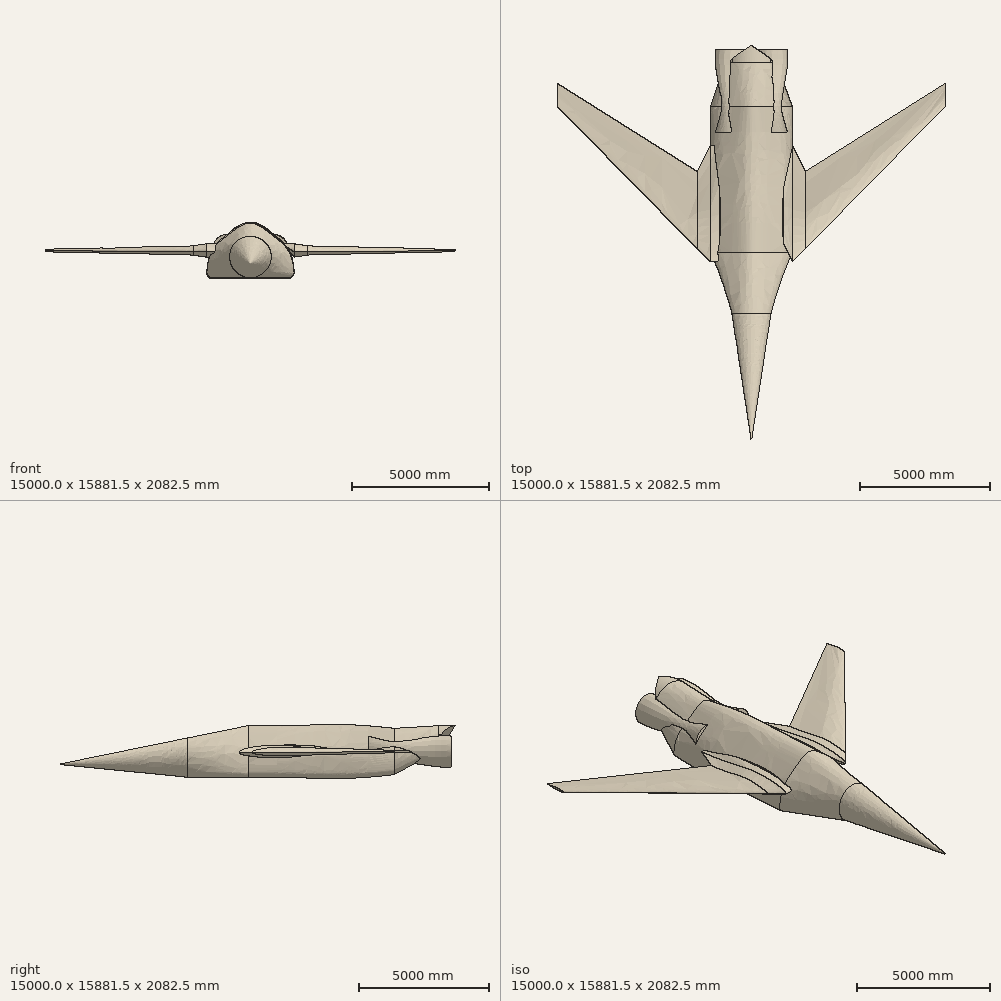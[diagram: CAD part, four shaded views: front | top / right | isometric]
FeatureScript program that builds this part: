
annotation { "Feature Type Name" : "Feature", "Feature Type Description" : "" }
export const myFeature = defineFeature(function(context is Context, id is Id, definition is map)
    precondition{}
    {
        {
            var Q0;
            Q0=qCreatedBy(makeId("Right.planeOp"),FACE);
            var sketch = newSketch(context, id + "F0", { "sketchPlane" : qUnion([Q0])});
            skLineSegment(sketch, "E0", {"start": v(0, 0) * mm, "end": v(-1750, 0) * mm});
            skLineSegment(sketch, "E1", {"start": v(-1750, 0) * mm, "end": v(-3500, 0) * mm});
            skLineSegment(sketch, "E2", {"start": v(-3500, 0) * mm, "end": v(-3500, -1000) * mm});
            skLineSegment(sketch, "E3", {"start": v(-3500, -1000) * mm, "end": v(-8500, -1000) * mm});
            skLineSegment(sketch, "E4", {"start": v(-8500, -1000) * mm, "end": v(-8500, -499.31) * mm});
            skLineSegment(sketch, "E5", {"start": v(-1151.4, 0) * mm, "end": v(-1151.4, 1000) * mm});
            skLineSegment(sketch, "E6", {"start": v(-1151.4, 1000) * mm, "end": v(-8500, -499.31) * mm});
            skLineSegment(sketch, "E7", {"start": v(-8500, -499.31) * mm, "end": v(-3500, -1000) * mm});
            skLineSegment(sketch, "E8", {"start": v(-3500, 0) * mm, "end": v(-3500, 520.82) * mm});
            skLineSegment(sketch, "E9", {"start": v(-8500, -499.31) * mm, "end": v(-8450, -499.31) * mm});
            skLineSegment(sketch, "E10", {"start": v(-8450, -499.31) * mm, "end": v(-8450, -489.1) * mm});
            skLineSegment(sketch, "E11", {"start": v(-8450, -499.31) * mm, "end": v(-8450, -504.32) * mm});
            skSolve(sketch);
        }
        {
            var Q0;
            Q0=sQuery(id+"F0.wireOp",EDGE,"E5");
            cPlane(context, id + "F1", {"entities" : qUnion([Q0]), "cplaneType" : CPlaneType.LINE_ANGLE, "offset" : 25 * mm, "angle" : 90 * degree, "oppositeDirection" : true, "width" : 150 * mm, "height" : 150 * mm});
        }
        {
            var Q0;
            Q0=qCreatedBy(id+"F1.planeOp",FACE);
            var sketch = newSketch(context, id + "F2", { "sketchPlane" : qUnion([Q0])});
            skLineSegment(sketch, "E12.top", {"start": v(-1394.2, -1000) * mm, "end": v(1394.2, -1000) * mm});
            skPoint(sketch, "E12.middle", {"position": v(0, 0) * mm});
            skFitSpline(sketch, "E13", {"points": [v(-1600, -1000) * mm, v(-848, 530) * mm, v(0, 1000) * mm, v(848, 530) * mm, v(1600, -1000) * mm], "startDerivative": vector(0, 10524.75) * mm, "endDerivative": vector(0, -10524.75) * mm});
            skArc(sketch, "E14", {"start": v(-735.27, 618.52) * mm, "mid": v(-1273.27, 435.52) * mm, "end": v(-1440.68, -107.53) * mm});
            skArc(sketch, "E15", {"start": v(1440.68, -107.53) * mm, "mid": v(1273.27, 435.52) * mm, "end": v(735.27, 618.52) * mm});
            skFitSpline(sketch, "E16.trimOffspring", {"points": [v(-1600, -1000) * mm, v(-848, 530) * mm, v(0, 1000) * mm, v(848, 530) * mm, v(1600, -1000) * mm], "startDerivative": vector(0, 10524.75) * mm, "endDerivative": vector(0, -10524.75) * mm});
            skFitSpline(sketch, "E17.trimOffspring", {"points": [v(-1600, -1000) * mm, v(-848, 530) * mm, v(0, 1000) * mm, v(848, 530) * mm, v(1600, -1000) * mm], "startDerivative": vector(0, 10524.75) * mm, "endDerivative": vector(0, -10524.75) * mm});
            skArc(sketch, "E18.filletArc", {"start": v(-1593.82, -787.83) * mm, "mid": v(-1539.85, -937.05) * mm, "end": v(-1394.2, -1000) * mm});
            skArc(sketch, "E19.filletArc", {"start": v(1394.2, -1000) * mm, "mid": v(1539.85, -937.05) * mm, "end": v(1593.82, -787.83) * mm});
            skSolve(sketch);
        }
        {
            var Q0;
            Q0=qCreatedBy(makeId("Front.planeOp"),FACE);
            var sketch = newSketch(context, id + "F3", { "sketchPlane" : qUnion([Q0])});
            skLineSegment(sketch, "E20.top", {"start": v(-1394.2, -1000) * mm, "end": v(1394.2, -1000) * mm});
            skPoint(sketch, "E20.middle", {"position": v(0, 0) * mm});
            skFitSpline(sketch, "E21", {"points": [v(-1600, -1000) * mm, v(-848, 530) * mm, v(0, 1000) * mm, v(848, 530) * mm, v(1600, -1000) * mm], "startDerivative": vector(0, 10524.75) * mm, "endDerivative": vector(0, -10524.75) * mm});
            skArc(sketch, "E22", {"start": v(-735.27, 618.52) * mm, "mid": v(-1273.27, 435.52) * mm, "end": v(-1440.68, -107.53) * mm});
            skArc(sketch, "E23", {"start": v(1440.68, -107.53) * mm, "mid": v(1273.27, 435.52) * mm, "end": v(735.27, 618.52) * mm});
            skFitSpline(sketch, "E24.trimOffspring", {"points": [v(-1600, -1000) * mm, v(-848, 530) * mm, v(0, 1000) * mm, v(848, 530) * mm, v(1600, -1000) * mm], "startDerivative": vector(0, 10524.75) * mm, "endDerivative": vector(0, -10524.75) * mm});
            skFitSpline(sketch, "E25.trimOffspring", {"points": [v(-1600, -1000) * mm, v(-848, 530) * mm, v(0, 1000) * mm, v(848, 530) * mm, v(1600, -1000) * mm], "startDerivative": vector(0, 10524.75) * mm, "endDerivative": vector(0, -10524.75) * mm});
            skArc(sketch, "E26.filletArc", {"start": v(-1593.82, -787.83) * mm, "mid": v(-1539.85, -937.05) * mm, "end": v(-1394.2, -1000) * mm});
            skArc(sketch, "E27.filletArc", {"start": v(1394.2, -1000) * mm, "mid": v(1539.85, -937.05) * mm, "end": v(1593.82, -787.83) * mm});
            skSolve(sketch);
        }
        {
            var Q0;
            Q0=qCreatedBy(makeId("Front.planeOp"),FACE);
            cPlane(context, id + "F4", {"entities" : qUnion([Q0]), "cplaneType" : CPlaneType.OFFSET, "offset" : 3500 * mm, "oppositeDirection" : true, "width" : 150 * mm, "height" : 150 * mm});
        }
        {
            var Q0;
            Q0=qCreatedBy(id+"F4.planeOp",FACE);
            var sketch = newSketch(context, id + "F5", { "sketchPlane" : qUnion([Q0])});
            skLineSegment(sketch, "E28.top", {"start": v(-1394.2, -1000) * mm, "end": v(1394.2, -1000) * mm});
            skPoint(sketch, "E28.middle", {"position": v(0, 0) * mm});
            skFitSpline(sketch, "E29", {"points": [v(-1600, -1000) * mm, v(-848, 530) * mm, v(0, 1000) * mm, v(848, 530) * mm, v(1600, -1000) * mm], "startDerivative": vector(0, 10524.75) * mm, "endDerivative": vector(0, -10524.75) * mm});
            skArc(sketch, "E30", {"start": v(-735.27, 618.52) * mm, "mid": v(-1273.27, 435.52) * mm, "end": v(-1440.68, -107.53) * mm});
            skArc(sketch, "E31", {"start": v(1440.68, -107.53) * mm, "mid": v(1273.27, 435.52) * mm, "end": v(735.27, 618.52) * mm});
            skFitSpline(sketch, "E32.trimOffspring", {"points": [v(-1600, -1000) * mm, v(-848, 530) * mm, v(0, 1000) * mm, v(848, 530) * mm, v(1600, -1000) * mm], "startDerivative": vector(0, 10524.75) * mm, "endDerivative": vector(0, -10524.75) * mm});
            skFitSpline(sketch, "E33.trimOffspring", {"points": [v(-1600, -1000) * mm, v(-848, 530) * mm, v(0, 1000) * mm, v(848, 530) * mm, v(1600, -1000) * mm], "startDerivative": vector(0, 10524.75) * mm, "endDerivative": vector(0, -10524.75) * mm});
            skArc(sketch, "E34.filletArc", {"start": v(-1593.82, -787.83) * mm, "mid": v(-1539.85, -937.05) * mm, "end": v(-1394.2, -1000) * mm});
            skArc(sketch, "E35.filletArc", {"start": v(1394.2, -1000) * mm, "mid": v(1539.85, -937.05) * mm, "end": v(1593.82, -787.83) * mm});
            skSolve(sketch);
        }
        {
            var Q0;
            Q0=qCreatedBy(makeId("Front.planeOp"),FACE);
            cPlane(context, id + "F6", {"entities" : qUnion([Q0]), "cplaneType" : CPlaneType.OFFSET, "offset" : 4500 * mm, "oppositeDirection" : true, "width" : 150 * mm, "height" : 150 * mm});
        }
        {
            var Q0;
            Q0=qCreatedBy(id+"F6.planeOp",FACE);
            var sketch = newSketch(context, id + "F7", { "sketchPlane" : qUnion([Q0])});
            skLineSegment(sketch, "E36.top", {"start": v(-1413.07, -900) * mm, "end": v(1413.07, -900) * mm});
            skPoint(sketch, "E36.middle", {"position": v(0, 0) * mm});
            skFitSpline(sketch, "E37", {"points": [v(-1600, -900) * mm, v(-784.42, 441.24) * mm, v(0, 900) * mm, v(784.42, 441.24) * mm, v(1600, -900) * mm], "startDerivative": vector(0, 9508.62) * mm, "endDerivative": vector(0, -9508.62) * mm});
            skArc(sketch, "E38", {"start": v(-719.25, 488.69) * mm, "mid": v(-1131.76, 394.84) * mm, "end": v(-1324.66, 18.33) * mm});
            skArc(sketch, "E39", {"start": v(1324.66, 18.33) * mm, "mid": v(1131.76, 394.84) * mm, "end": v(719.25, 488.69) * mm});
            skFitSpline(sketch, "E40.trimOffspring", {"points": [v(-1600, -900) * mm, v(-784.42, 441.24) * mm, v(0, 900) * mm, v(784.42, 441.24) * mm, v(1600, -900) * mm], "startDerivative": vector(0, 9508.62) * mm, "endDerivative": vector(0, -9508.62) * mm});
            skFitSpline(sketch, "E41.trimOffspring", {"points": [v(-1600, -900) * mm, v(-784.42, 441.24) * mm, v(0, 900) * mm, v(784.42, 441.24) * mm, v(1600, -900) * mm], "startDerivative": vector(0, 9508.62) * mm, "endDerivative": vector(0, -9508.62) * mm});
            skArc(sketch, "E42.filletArc", {"start": v(-1592.48, -705.43) * mm, "mid": v(-1545.4, -842.02) * mm, "end": v(-1413.07, -900) * mm});
            skArc(sketch, "E43.filletArc", {"start": v(1413.07, -900) * mm, "mid": v(1545.4, -842.02) * mm, "end": v(1592.48, -705.43) * mm});
            skLineSegment(sketch, "E44", {"start": v(-719.25, 488.69) * mm, "end": v(-1324.66, 18.33) * mm, "construction": true});
            skLineSegment(sketch, "E45", {"start": v(719.25, 488.69) * mm, "end": v(1324.66, 18.33) * mm, "construction": true});
            skSolve(sketch);
        }
        {
            var Q0;
            Q0=qCreatedBy(makeId("Front.planeOp"),FACE);
            cPlane(context, id + "F8", {"entities" : qUnion([Q0]), "cplaneType" : CPlaneType.OFFSET, "offset" : 6232.05 * mm, "oppositeDirection" : true, "width" : 150 * mm, "height" : 150 * mm});
        }
        {
            var Q0;
            Q0=qCreatedBy(id+"F8.planeOp",FACE);
            var sketch = newSketch(context, id + "F9", { "sketchPlane" : qUnion([Q0])});
            skArc(sketch, "E46", {"start": v(998.61, 52.63) * mm, "mid": v(0, 1000) * mm, "end": v(-998.61, 52.63) * mm});
            skLineSegment(sketch, "E47", {"start": v(0, 0) * mm, "end": v(-948.68, 0) * mm});
            skLineSegment(sketch, "E48", {"start": v(0, 0) * mm, "end": v(948.68, 0) * mm});
            skLineSegment(sketch, "E49", {"start": v(0, 1000) * mm, "end": v(0, 675) * mm, "construction": true});
            skLineSegment(sketch, "E50", {"start": v(0, 675) * mm, "end": v(-737.82, 675) * mm, "construction": true});
            skLineSegment(sketch, "E51", {"start": v(0, 675) * mm, "end": v(737.82, 675) * mm, "construction": true});
            skPoint(sketch, "E52.visualSharp", {"position": v(-1000, 0) * mm});
            skArc(sketch, "E52.filletArc", {"start": v(-998.61, 52.63) * mm, "mid": v(-984.96, 15.59) * mm, "end": v(-948.68, 0) * mm});
            skPoint(sketch, "E53.visualSharp", {"position": v(1000, 0) * mm});
            skArc(sketch, "E53.filletArc", {"start": v(948.68, 0) * mm, "mid": v(984.96, 15.59) * mm, "end": v(998.61, 52.63) * mm});
            skSolve(sketch);
        }
        {
            var Q0;
            Q0=makeQuery(id+"F2.imprint","IMPRINT",FACE,{"disambiguationData":[TD([[makeQuery(id+"F2.imprint","IMPRINT",EDGE,{"derivedFrom":sQuery(id+"F2.wireOp",EDGE,"E12.top")}),1.0]])]});
            var Q1;
            Q1=makeQuery(id+"F3.imprint","IMPRINT",FACE,{"disambiguationData":[TD([[makeQuery(id+"F3.imprint","IMPRINT",EDGE,{"derivedFrom":sQuery(id+"F3.wireOp",EDGE,"E20.top")}),1.0]])]});
            var Q2;
            Q2=makeQuery(id+"F5.imprint","IMPRINT",FACE,{"disambiguationData":[TD([[makeQuery(id+"F5.imprint","IMPRINT",EDGE,{"derivedFrom":sQuery(id+"F5.wireOp",EDGE,"E28.top")}),1.0]])]});
            var Q3;
            Q3=makeQuery(id+"F7.imprint","IMPRINT",FACE,{"disambiguationData":[TD([[makeQuery(id+"F7.imprint","IMPRINT",EDGE,{"derivedFrom":sQuery(id+"F7.wireOp",EDGE,"E36.top")}),1.0]])]});
            loft(context, id + "F10", {"sheetProfilesArray" : [{ "sheetProfileEntities" : qUnion([Q0]) }, { "sheetProfileEntities" : qUnion([Q1]) }, { "sheetProfileEntities" : qUnion([Q2]) }, { "sheetProfileEntities" : qUnion([Q3]) }]});
        }
        {
            var Q0;
            Q0=sQuery(id+"F7.wireOp",EDGE,"E44");
            var Q1;
            Q1=sQuery(id+"F9.wireOp",VERTEX,"E50.end");
            cPlane(context, id + "F11", {"entities" : qUnion([Q0, Q1]), "cplaneType" : CPlaneType.LINE_ANGLE, "offset" : 25 * mm, "angle" : 180 * degree, "width" : 150 * mm, "height" : 150 * mm});
        }
        {
            var Q0;
            Q0=qCreatedBy(id+"F11.planeOp",FACE);
            var sketch = newSketch(context, id + "F12", { "sketchPlane" : qUnion([Q0])});
            skLineSegment(sketch, "E54", {"start": v(-589.34, 4526.34) * mm, "end": v(-612.8, 6268.32) * mm});
            skLineSegment(sketch, "E55", {"start": v(-1354.08, 4472.19) * mm, "end": v(-612.8, 6268.32) * mm});
            skSolve(sketch);
        }
        {
            var Q0;
            Q0=sQuery(id+"F7.wireOp",EDGE,"E45");
            var Q1;
            Q1=sQuery(id+"F9.wireOp",VERTEX,"E51.end");
            cPlane(context, id + "F13", {"entities" : qUnion([Q0, Q1]), "cplaneType" : CPlaneType.LINE_ANGLE, "offset" : 25 * mm, "angle" : 0 * degree, "width" : 150 * mm, "height" : 150 * mm});
        }
        {
            var Q0;
            Q0=qCreatedBy(id+"F13.planeOp",FACE);
            var sketch = newSketch(context, id + "F14", { "sketchPlane" : qUnion([Q0])});
            skLineSegment(sketch, "E56", {"start": v(589.34, 4526.34) * mm, "end": v(612.8, 6268.32) * mm});
            skLineSegment(sketch, "E57", {"start": v(1354.08, 4472.19) * mm, "end": v(612.8, 6268.32) * mm});
            skSolve(sketch);
        }
        {
            var Q1;
            Q1=makeQuery(id+"F10.opLoft","CAP_FACE",FACE,{"disambiguationData":[OSD([makeQuery(id+"F7.imprint","IMPRINT",FACE,{"disambiguationData":[TD([[makeQuery(id+"F7.imprint","IMPRINT",EDGE,{"derivedFrom":sQuery(id+"F7.wireOp",EDGE,"E36.top")}),1.0]])]})])],"isStart":true});
            var Q2;
            Q2=makeQuery(id+"F9.imprint","IMPRINT",FACE,{"disambiguationData":[TD([[makeQuery(id+"F9.imprint","IMPRINT",EDGE,{"derivedFrom":sQuery(id+"F9.wireOp",EDGE,"E46")}),1.0]])]});
            var Q3;
            Q3=sQuery(id+"F12.wireOp",EDGE,"E54");
            var Q4;
            Q4=sQuery(id+"F14.wireOp",EDGE,"E56");
            loft(context, id + "F15", {"operationType" : NewBodyOperationType.ADD, "addGuides" : true, "sheetProfilesArray" : [{ "sheetProfileEntities" : qUnion([Q1]) }, { "sheetProfileEntities" : qUnion([Q2]) }], "guidesArray" : [{ "guideEntities" : qUnion([Q3]), "guideDerivativeType" : LoftGuideDerivativeType.DEFAULT, "guideDerivativeMagnitude" : 1 }, { "guideEntities" : qUnion([Q4]), "guideDerivativeType" : LoftGuideDerivativeType.DEFAULT, "guideDerivativeMagnitude" : 1 }]});
        }
        {
            var Q0;
            Q0=makeQuery(id+"F15.opLoft","CAP_FACE",FACE,{"disambiguationData":[OSD([makeQuery(id+"F9.imprint","IMPRINT",FACE,{"disambiguationData":[TD([[makeQuery(id+"F9.imprint","IMPRINT",EDGE,{"derivedFrom":sQuery(id+"F9.wireOp",EDGE,"E46")}),1.0]])]})])],"isStart":true});
            extrude(context, id + "F16", {"entities" : qUnion([Q0]), "operationType" : NewBodyOperationType.ADD, "depth" : 649.4 * mm, "offsetDistance" : 25 * mm});
        }
        {
            var Q0;
            Q0=qCreatedBy(makeId("Right.planeOp"),FACE);
            var sketch = newSketch(context, id + "F17", { "sketchPlane" : qUnion([Q0])});
            skLineSegment(sketch, "E58", {"start": v(0, 0) * mm, "end": v(4500, 0) * mm});
            skLineSegment(sketch, "E59", {"start": v(4500, 0) * mm, "end": v(6232.05, 0) * mm});
            skLineSegment(sketch, "E60", {"start": v(4500, 0) * mm, "end": v(4500, 1000) * mm});
            skLineSegment(sketch, "E61", {"start": v(4500, 1000) * mm, "end": v(6881.46, 1000) * mm});
            skLineSegment(sketch, "E62", {"start": v(6881.46, 1000) * mm, "end": v(6881.46, -1000) * mm});
            skLineSegment(sketch, "E63", {"start": v(6881.46, 1000) * mm, "end": v(6232.05, 0) * mm});
            skLineSegment(sketch, "E64", {"start": v(6232.05, 0) * mm, "end": v(5582.64, -1000) * mm});
            skLineSegment(sketch, "E65", {"start": v(5582.64, -1000) * mm, "end": v(6881.46, -1000) * mm});
            skSolve(sketch);
        }
        {
            var Q0;
            Q0=makeQuery(id+"F17.imprint","IMPRINT",FACE,{"disambiguationData":[TD([[makeQuery(id+"F17.imprint","IMPRINT",EDGE,{"derivedFrom":sQuery(id+"F17.wireOp",EDGE,"E62")}),-1.0]])]});
            var Q1;
            Q1=sQuery(id+"F17.wireOp",EDGE,"E61");
            revolve(context, id + "F18", {"operationType" : NewBodyOperationType.REMOVE, "entities" : qUnion([Q0]), "axis" : qUnion([Q1]), "revolveType" : RevolveType.SYMMETRIC, "oppositeDirection" : true, "angle" : 182 * degree});
        }
        {
            var Q0;
            Q0=qCreatedBy(id+"F1.planeOp",FACE);
            var sketch = newSketch(context, id + "F19", { "sketchPlane" : qUnion([Q0])});
            skLineSegment(sketch, "E66.top", {"start": v(-1394.2, -1000) * mm, "end": v(1394.2, -1000) * mm});
            skPoint(sketch, "E66.middle", {"position": v(0, 0) * mm});
            skFitSpline(sketch, "E67", {"points": [v(-1600, -1000) * mm, v(-848, 530) * mm, v(0, 1000) * mm, v(848, 530) * mm, v(1600, -1000) * mm], "startDerivative": vector(0, 10524.75) * mm, "endDerivative": vector(0, -10524.75) * mm});
            skArc(sketch, "E68.filletArc", {"start": v(-1593.82, -787.83) * mm, "mid": v(-1539.85, -937.05) * mm, "end": v(-1394.2, -1000) * mm});
            skArc(sketch, "E69.filletArc", {"start": v(1394.2, -1000) * mm, "mid": v(1539.85, -937.05) * mm, "end": v(1593.82, -787.83) * mm});
            skLineSegment(sketch, "E70", {"start": v(-1593.82, -787.83) * mm, "end": v(-1394.2, -1000) * mm, "construction": true});
            skLineSegment(sketch, "E71", {"start": v(1593.82, -787.83) * mm, "end": v(1394.2, -1000) * mm, "construction": true});
            skSolve(sketch);
        }
        {
            var Q0;
            Q0=qCreatedBy(makeId("Front.planeOp"),FACE);
            cPlane(context, id + "F20", {"entities" : qUnion([Q0]), "cplaneType" : CPlaneType.OFFSET, "offset" : 3500 * mm, "width" : 150 * mm, "height" : 150 * mm});
        }
        {
            var Q0;
            Q0=qCreatedBy(id+"F20.planeOp",FACE);
            var sketch = newSketch(context, id + "F21", { "sketchPlane" : qUnion([Q0])});
            skCircle(sketch, "E72", {"center": v(0, -239.59) * mm, "radius": 760.41 * mm});
            skLineSegment(sketch, "E73", {"start": v(0, -1000) * mm, "end": v(0, -800) * mm, "construction": true});
            skLineSegment(sketch, "E74", {"start": v(0, -800) * mm, "end": v(-513.97, -800) * mm, "construction": true});
            skLineSegment(sketch, "E75", {"start": v(0, -800) * mm, "end": v(513.97, -800) * mm, "construction": true});
            skSolve(sketch);
        }
        {
            var Q0;
            Q0=qCreatedBy(makeId("Front.planeOp"),FACE);
            cPlane(context, id + "F22", {"entities" : qUnion([Q0]), "cplaneType" : CPlaneType.OFFSET, "offset" : 8450 * mm, "width" : 150 * mm, "height" : 150 * mm});
        }
        {
            var Q0;
            Q0=qCreatedBy(id+"F22.planeOp",FACE);
            var sketch = newSketch(context, id + "F23", { "sketchPlane" : qUnion([Q0])});
            skCircle(sketch, "E76", {"center": v(0, -496.71) * mm, "radius": 7.6 * mm});
            skSolve(sketch);
        }
        {
            var Q0;
            Q0=sQuery(id+"F19.wireOp",EDGE,"E70");
            var Q1;
            Q1=sQuery(id+"F21.wireOp",VERTEX,"E74.end");
            cPlane(context, id + "F24", {"entities" : qUnion([Q0, Q1]), "cplaneType" : CPlaneType.LINE_ANGLE, "offset" : 25 * mm, "angle" : 0 * degree, "width" : 150 * mm, "height" : 150 * mm});
        }
        {
            var Q0;
            Q0=qCreatedBy(id+"F24.planeOp",FACE);
            var sketch = newSketch(context, id + "F25", { "sketchPlane" : qUnion([Q0])});
            skLineSegment(sketch, "E77", {"start": v(3032.27, -230.44) * mm, "end": v(558.11, 518.4) * mm});
            skLineSegment(sketch, "E78", {"start": v(3032.27, -230.44) * mm, "end": v(558.11, 227.09) * mm});
            skSolve(sketch);
        }
        {
            var Q0;
            Q0=sQuery(id+"F19.wireOp",EDGE,"E71");
            var Q1;
            Q1=sQuery(id+"F21.wireOp",VERTEX,"E75.end");
            cPlane(context, id + "F26", {"entities" : qUnion([Q0, Q1]), "cplaneType" : CPlaneType.LINE_ANGLE, "offset" : 25 * mm, "angle" : 180 * degree, "width" : 150 * mm, "height" : 150 * mm});
        }
        {
            var Q0;
            Q0=qCreatedBy(id+"F26.planeOp",FACE);
            var sketch = newSketch(context, id + "F27", { "sketchPlane" : qUnion([Q0])});
            skLineSegment(sketch, "E79", {"start": v(-3032.27, -230.44) * mm, "end": v(-558.11, 518.4) * mm});
            skLineSegment(sketch, "E80", {"start": v(-3032.27, -230.44) * mm, "end": v(-558.11, 227.09) * mm});
            skSolve(sketch);
        }
        {
            var Q1;
            Q1=makeQuery(id+"F19.imprint","IMPRINT",FACE,{"disambiguationData":[TD([[makeQuery(id+"F19.imprint","IMPRINT",EDGE,{"derivedFrom":sQuery(id+"F19.wireOp",EDGE,"E66.top")}),1.0]])]});
            var Q2;
            Q2=makeQuery(id+"F21.imprint","IMPRINT",FACE,{"disambiguationData":[TD([[makeQuery(id+"F21.imprint","IMPRINT",EDGE,{"derivedFrom":sQuery(id+"F21.wireOp",EDGE,"E72")}),1.0]])]});
            var Q3;
            Q3=sQuery(id+"F25.wireOp",EDGE,"E77");
            var Q4;
            Q4=sQuery(id+"F27.wireOp",EDGE,"E79");
            loft(context, id + "F28", {"operationType" : NewBodyOperationType.ADD, "addGuides" : true, "sheetProfilesArray" : [{ "sheetProfileEntities" : qUnion([Q1]) }, { "sheetProfileEntities" : qUnion([Q2]) }], "guidesArray" : [{ "guideEntities" : qUnion([Q3]), "guideDerivativeType" : LoftGuideDerivativeType.DEFAULT, "guideDerivativeMagnitude" : 1 }, { "guideEntities" : qUnion([Q4]), "guideDerivativeType" : LoftGuideDerivativeType.DEFAULT, "guideDerivativeMagnitude" : 1 }]});
        }
        {
            var Q1;
            Q1=makeQuery(id+"F28.opLoft","CAP_FACE",FACE,{"disambiguationData":[OSD([makeQuery(id+"F21.imprint","IMPRINT",FACE,{"disambiguationData":[TD([[makeQuery(id+"F21.imprint","IMPRINT",EDGE,{"derivedFrom":sQuery(id+"F21.wireOp",EDGE,"E72")}),1.0]])]})])],"isStart":true});
            var Q2;
            Q2=makeQuery(id+"F23.imprint","IMPRINT",FACE,{"disambiguationData":[TD([[makeQuery(id+"F23.imprint","IMPRINT",EDGE,{"derivedFrom":sQuery(id+"F23.wireOp",EDGE,"E76")}),1.0]])]});
            loft(context, id + "F29", {"operationType" : NewBodyOperationType.ADD, "sheetProfilesArray" : [{ "sheetProfileEntities" : qUnion([Q1]) }, { "sheetProfileEntities" : qUnion([Q2]) }]});
        }
        {
            var Q0;
            Q0=makeQuery(id+"F29.opLoft","CAP_FACE",FACE,{"disambiguationData":[OSD([makeQuery(id+"F23.imprint","IMPRINT",FACE,{"disambiguationData":[TD([[makeQuery(id+"F23.imprint","IMPRINT",EDGE,{"derivedFrom":sQuery(id+"F23.wireOp",EDGE,"E76")}),1.0]])]})])],"isStart":true});
            extrude(context, id + "F30", {"entities" : qUnion([Q0]), "operationType" : NewBodyOperationType.ADD, "depth" : 550 * mm, "offsetDistance" : 25 * mm});
        }
        {
            var Q0;
            Q0=qCreatedBy(makeId("Front.planeOp"),FACE);
            cPlane(context, id + "F31", {"entities" : qUnion([Q0]), "cplaneType" : CPlaneType.OFFSET, "offset" : 3500 * mm, "oppositeDirection" : true, "width" : 150 * mm, "height" : 150 * mm});
        }
        {
            var Q0;
            Q0=qCreatedBy(id+"F31.planeOp",FACE);
            var sketch = newSketch(context, id + "F32", { "sketchPlane" : qUnion([Q0])});
            skCircle(sketch, "E81", {"center": v(-800, 0) * mm, "radius": 600 * mm});
            skCircle(sketch, "E82", {"center": v(800, 0) * mm, "radius": 600 * mm});
            skSolve(sketch);
        }
        {
            var Q0;
            Q0=qCreatedBy(makeId("Front.planeOp"),FACE);
            cPlane(context, id + "F33", {"entities" : qUnion([Q0]), "cplaneType" : CPlaneType.OFFSET, "offset" : 4500 * mm, "oppositeDirection" : true, "width" : 150 * mm, "height" : 150 * mm});
        }
        {
            var Q0;
            Q0=qCreatedBy(id+"F33.planeOp",FACE);
            var sketch = newSketch(context, id + "F34", { "sketchPlane" : qUnion([Q0])});
            skCircle(sketch, "E83", {"center": v(-800, 0) * mm, "radius": 400 * mm});
            skCircle(sketch, "E84", {"center": v(800, 0) * mm, "radius": 400 * mm});
            skSolve(sketch);
        }
        {
            var Q0;
            Q0=qCreatedBy(makeId("Front.planeOp"),FACE);
            cPlane(context, id + "F35", {"entities" : qUnion([Q0]), "cplaneType" : CPlaneType.OFFSET, "offset" : 6232.05 * mm, "oppositeDirection" : true, "width" : 150 * mm, "height" : 150 * mm});
        }
        {
            var Q0;
            Q0=qCreatedBy(id+"F35.planeOp",FACE);
            var sketch = newSketch(context, id + "F36", { "sketchPlane" : qUnion([Q0])});
            skCircle(sketch, "E85", {"center": v(-800, 0) * mm, "radius": 600 * mm});
            skCircle(sketch, "E86", {"center": v(800, 0) * mm, "radius": 600 * mm});
            skSolve(sketch);
        }
        {
            var Q0;
            Q0=qCreatedBy(makeId("Front.planeOp"),FACE);
            cPlane(context, id + "F37", {"entities" : qUnion([Q0]), "cplaneType" : CPlaneType.OFFSET, "offset" : 6732.05 * mm, "oppositeDirection" : true, "width" : 150 * mm, "height" : 150 * mm});
        }
        {
            var Q0;
            Q0=qCreatedBy(id+"F37.planeOp",FACE);
            var sketch = newSketch(context, id + "F38", { "sketchPlane" : qUnion([Q0])});
            skCircle(sketch, "E87", {"center": v(-800, 0) * mm, "radius": 600 * mm});
            skCircle(sketch, "E88", {"center": v(800, 0) * mm, "radius": 600 * mm});
            skSolve(sketch);
        }
        {
            var Q0;
            Q0=makeQuery(id+"F32.imprint","IMPRINT",FACE,{"disambiguationData":[TD([[makeQuery(id+"F32.imprint","IMPRINT",EDGE,{"derivedFrom":sQuery(id+"F32.wireOp",EDGE,"E81")}),1.0]])]});
            var Q1;
            Q1=makeQuery(id+"F34.imprint","IMPRINT",FACE,{"disambiguationData":[TD([[makeQuery(id+"F34.imprint","IMPRINT",EDGE,{"derivedFrom":sQuery(id+"F34.wireOp",EDGE,"E83")}),1.0]])]});
            var Q2;
            Q2=makeQuery(id+"F36.imprint","IMPRINT",FACE,{"disambiguationData":[TD([[makeQuery(id+"F36.imprint","IMPRINT",EDGE,{"derivedFrom":sQuery(id+"F36.wireOp",EDGE,"E85")}),1.0]])]});
            var Q3;
            Q3=makeQuery(id+"F38.imprint","IMPRINT",FACE,{"disambiguationData":[TD([[makeQuery(id+"F38.imprint","IMPRINT",EDGE,{"derivedFrom":sQuery(id+"F38.wireOp",EDGE,"E87")}),1.0]])]});
            loft(context, id + "F39", {"sheetProfilesArray" : [{ "sheetProfileEntities" : qUnion([Q0]) }, { "sheetProfileEntities" : qUnion([Q1]) }, { "sheetProfileEntities" : qUnion([Q2]) }, { "sheetProfileEntities" : qUnion([Q3]) }]});
        }
        {
            var Q0;
            Q0=makeQuery(id+"F32.imprint","IMPRINT",FACE,{"disambiguationData":[TD([[makeQuery(id+"F32.imprint","IMPRINT",EDGE,{"derivedFrom":sQuery(id+"F32.wireOp",EDGE,"E82")}),1.0]])]});
            var Q1;
            Q1=makeQuery(id+"F34.imprint","IMPRINT",FACE,{"disambiguationData":[TD([[makeQuery(id+"F34.imprint","IMPRINT",EDGE,{"derivedFrom":sQuery(id+"F34.wireOp",EDGE,"E84")}),1.0]])]});
            var Q2;
            Q2=makeQuery(id+"F36.imprint","IMPRINT",FACE,{"disambiguationData":[TD([[makeQuery(id+"F36.imprint","IMPRINT",EDGE,{"derivedFrom":sQuery(id+"F36.wireOp",EDGE,"E86")}),1.0]])]});
            var Q3;
            Q3=makeQuery(id+"F38.imprint","IMPRINT",FACE,{"disambiguationData":[TD([[makeQuery(id+"F38.imprint","IMPRINT",EDGE,{"derivedFrom":sQuery(id+"F38.wireOp",EDGE,"E88")}),1.0]])]});
            loft(context, id + "F40", {"sheetProfilesArray" : [{ "sheetProfileEntities" : qUnion([Q0]) }, { "sheetProfileEntities" : qUnion([Q1]) }, { "sheetProfileEntities" : qUnion([Q2]) }, { "sheetProfileEntities" : qUnion([Q3]) }]});
        }
        {
            var Q0;
            Q0=qCreatedBy(makeId("Right.planeOp"),FACE);
            var sketch = newSketch(context, id + "F41", { "sketchPlane" : qUnion([Q0])});
            skFitSpline(sketch, "E89", {"points": [v(-1500, -50) * mm, v(0, 250) * mm, v(3000, -50) * mm, v(0, -250) * mm, v(-1500, -50) * mm]});
            skSolve(sketch);
        }
        {
            var Q0;
            Q0=qCreatedBy(makeId("Right.planeOp"),FACE);
            cPlane(context, id + "F42", {"entities" : qUnion([Q0]), "cplaneType" : CPlaneType.OFFSET, "offset" : 1600 * mm, "oppositeDirection" : true, "width" : 150 * mm, "height" : 150 * mm});
        }
        {
            var Q0;
            Q0=qCreatedBy(id+"F42.planeOp",FACE);
            var sketch = newSketch(context, id + "F43", { "sketchPlane" : qUnion([Q0])});
            skFitSpline(sketch, "E90", {"points": [v(-1500, -50) * mm, v(0, 250) * mm, v(3000, -50) * mm], "startDerivative": vector(0, 1247.63) * mm, "endDerivative": vector(7705.35, -256.85) * mm});
            skFitSpline(sketch, "E91", {"points": [v(-1500, -50) * mm, v(0, -250) * mm, v(3000, -50) * mm], "startDerivative": vector(0, -722.87) * mm, "endDerivative": vector(7692.49, -256.42) * mm});
            skSolve(sketch);
        }
        {
            var Q0;
            Q0=qCreatedBy(makeId("Right.planeOp"),FACE);
            cPlane(context, id + "F44", {"entities" : qUnion([Q0]), "cplaneType" : CPlaneType.OFFSET, "offset" : 1600 * mm, "width" : 150 * mm, "height" : 150 * mm});
        }
        {
            var Q0;
            Q0=qCreatedBy(id+"F44.planeOp",FACE);
            var sketch = newSketch(context, id + "F45", { "sketchPlane" : qUnion([Q0])});
            skFitSpline(sketch, "E92", {"points": [v(-1500, -50) * mm, v(0, 250) * mm, v(3000, -50) * mm], "startDerivative": vector(0, 1247.63) * mm, "endDerivative": vector(7705.35, -256.85) * mm});
            skFitSpline(sketch, "E93", {"points": [v(-1500, -50) * mm, v(0, -250) * mm, v(3000, -50) * mm], "startDerivative": vector(0, -722.87) * mm, "endDerivative": vector(7692.49, -256.42) * mm});
            skSolve(sketch);
        }
        {
            var Q0;
            Q0=qCreatedBy(makeId("Right.planeOp"),FACE);
            cPlane(context, id + "F46", {"entities" : qUnion([Q0]), "cplaneType" : CPlaneType.OFFSET, "offset" : 2100 * mm, "oppositeDirection" : true, "width" : 150 * mm, "height" : 150 * mm});
        }
        {
            var Q0;
            Q0=qCreatedBy(id+"F46.planeOp",FACE);
            var sketch = newSketch(context, id + "F47", { "sketchPlane" : qUnion([Q0])});
            skFitSpline(sketch, "E94", {"points": [v(-1000, -36) * mm, v(0, 170) * mm, v(2000, -36) * mm], "startDerivative": vector(0, 576.8) * mm, "endDerivative": vector(5137.83, -184.96) * mm});
            skFitSpline(sketch, "E95", {"points": [v(-1000, -36) * mm, v(0, -170) * mm, v(2000, -36) * mm], "startDerivative": vector(0, -484.31) * mm, "endDerivative": vector(5128.4, -184.62) * mm});
            skSolve(sketch);
        }
        {
            var Q0;
            Q0=qCreatedBy(makeId("Right.planeOp"),FACE);
            cPlane(context, id + "F48", {"entities" : qUnion([Q0]), "cplaneType" : CPlaneType.OFFSET, "offset" : 2100 * mm, "width" : 150 * mm, "height" : 150 * mm});
        }
        {
            var Q0;
            Q0=qCreatedBy(id+"F48.planeOp",FACE);
            var sketch = newSketch(context, id + "F49", { "sketchPlane" : qUnion([Q0])});
            skFitSpline(sketch, "E96", {"points": [v(-1000, -36) * mm, v(0, 170) * mm, v(2000, -36) * mm], "startDerivative": vector(0, 576.8) * mm, "endDerivative": vector(5137.83, -184.96) * mm});
            skFitSpline(sketch, "E97", {"points": [v(-1000, -36) * mm, v(0, -170) * mm, v(2000, -36) * mm], "startDerivative": vector(0, -484.31) * mm, "endDerivative": vector(5128.4, -184.62) * mm});
            skSolve(sketch);
        }
        {
            var Q0;
            Q0=qCreatedBy(makeId("Right.planeOp"),FACE);
            cPlane(context, id + "F50", {"entities" : qUnion([Q0]), "cplaneType" : CPlaneType.OFFSET, "offset" : 7500 * mm, "oppositeDirection" : true, "width" : 150 * mm, "height" : 150 * mm});
        }
        {
            var Q0;
            Q0=qCreatedBy(id+"F50.planeOp",FACE);
            var sketch = newSketch(context, id + "F51", { "sketchPlane" : qUnion([Q0])});
            skFitSpline(sketch, "E98", {"points": [v(4500, -10) * mm, v(4800, 50) * mm, v(5400, -10) * mm], "startDerivative": vector(0, 177.4) * mm, "endDerivative": vector(1541.07, -51.37) * mm});
            skFitSpline(sketch, "E99", {"points": [v(4500, -10) * mm, v(4800, -50) * mm, v(5400, -10) * mm], "startDerivative": vector(0, -144.57) * mm, "endDerivative": vector(1538.5, -51.28) * mm});
            skSolve(sketch);
        }
        {
            var Q0;
            Q0=qCreatedBy(makeId("Right.planeOp"),FACE);
            cPlane(context, id + "F52", {"entities" : qUnion([Q0]), "cplaneType" : CPlaneType.OFFSET, "offset" : 7500 * mm, "width" : 150 * mm, "height" : 150 * mm});
        }
        {
            var Q0;
            Q0=qCreatedBy(id+"F52.planeOp",FACE);
            var sketch = newSketch(context, id + "F53", { "sketchPlane" : qUnion([Q0])});
            skFitSpline(sketch, "E100", {"points": [v(4500, -10) * mm, v(4800, 50) * mm, v(5400, -10) * mm], "startDerivative": vector(0, 177.4) * mm, "endDerivative": vector(1541.07, -51.37) * mm});
            skFitSpline(sketch, "E101", {"points": [v(4500, -10) * mm, v(4800, -50) * mm, v(5400, -10) * mm], "startDerivative": vector(0, -144.57) * mm, "endDerivative": vector(1538.5, -51.28) * mm});
            skSolve(sketch);
        }
        {
            var Q0;
            Q0=qSketchRegion(id+"F41",true);
            extrude(context, id + "F54", {"entities" : qUnion([Q0]), "endBound" : BoundingType.SYMMETRIC, "depth" : 2500 * mm, "offsetDistance" : 25 * mm});
        }
        {
            var Q1;
            Q1=makeQuery(id+"F54.opExtrude","CAP_FACE",FACE,{"disambiguationData":[OSD([sQuery(id+"F41.wireOp",EDGE,"E89")])],"isStart":true});
            var Q2;
            {var subQ0=sQuery(id+"F43.wireOp",EDGE,"E90");Q2=makeQuery(id+"F43.imprint","IMPRINT",FACE,{"disambiguationData":[TD([[makeQuery(id+"F43.imprint","IMPRINT",EDGE,{"derivedFrom":subQ0}),-1.0]])]});}
            loft(context, id + "F55", {"operationType" : NewBodyOperationType.ADD, "sheetProfilesArray" : [{ "sheetProfileEntities" : qUnion([Q1]) }, { "sheetProfileEntities" : qUnion([Q2]) }]});
        }
        {
            var Q1;
            Q1=makeQuery(id+"F54.opExtrude","CAP_FACE",FACE,{"disambiguationData":[OSD([sQuery(id+"F41.wireOp",EDGE,"E89")])],"isStart":false});
            var Q2;
            {var subQ0=sQuery(id+"F45.wireOp",EDGE,"E92");Q2=makeQuery(id+"F45.imprint","IMPRINT",FACE,{"disambiguationData":[TD([[makeQuery(id+"F45.imprint","IMPRINT",EDGE,{"derivedFrom":subQ0}),-1.0]])]});}
            loft(context, id + "F56", {"operationType" : NewBodyOperationType.ADD, "sheetProfilesArray" : [{ "sheetProfileEntities" : qUnion([Q1]) }, { "sheetProfileEntities" : qUnion([Q2]) }]});
        }
        {
            var Q1;
            {var subQ0=sQuery(id+"F43.wireOp",EDGE,"E90");Q1=makeQuery(id+"F55.opLoft","CAP_FACE",FACE,{"disambiguationData":[OSD([makeQuery(id+"F43.imprint","IMPRINT",FACE,{"disambiguationData":[TD([[makeQuery(id+"F43.imprint","IMPRINT",EDGE,{"derivedFrom":subQ0}),-1.0]])]})])],"isStart":true});}
            var Q2;
            {var subQ0=sQuery(id+"F47.wireOp",EDGE,"E94");Q2=makeQuery(id+"F47.imprint","IMPRINT",FACE,{"disambiguationData":[TD([[makeQuery(id+"F47.imprint","IMPRINT",EDGE,{"derivedFrom":subQ0}),-1.0]])]});}
            loft(context, id + "F57", {"operationType" : NewBodyOperationType.ADD, "sheetProfilesArray" : [{ "sheetProfileEntities" : qUnion([Q1]) }, { "sheetProfileEntities" : qUnion([Q2]) }]});
        }
        {
            var Q1;
            {var subQ0=sQuery(id+"F45.wireOp",EDGE,"E92");Q1=makeQuery(id+"F56.opLoft","CAP_FACE",FACE,{"disambiguationData":[OSD([makeQuery(id+"F45.imprint","IMPRINT",FACE,{"disambiguationData":[TD([[makeQuery(id+"F45.imprint","IMPRINT",EDGE,{"derivedFrom":subQ0}),-1.0]])]})])],"isStart":true});}
            var Q2;
            {var subQ0=sQuery(id+"F49.wireOp",EDGE,"E96");Q2=makeQuery(id+"F49.imprint","IMPRINT",FACE,{"disambiguationData":[TD([[makeQuery(id+"F49.imprint","IMPRINT",EDGE,{"derivedFrom":subQ0}),-1.0]])]});}
            loft(context, id + "F58", {"operationType" : NewBodyOperationType.ADD, "sheetProfilesArray" : [{ "sheetProfileEntities" : qUnion([Q1]) }, { "sheetProfileEntities" : qUnion([Q2]) }]});
        }
        {
            var Q1;
            {var subQ0=sQuery(id+"F47.wireOp",EDGE,"E94");Q1=makeQuery(id+"F57.opLoft","CAP_FACE",FACE,{"disambiguationData":[OSD([makeQuery(id+"F47.imprint","IMPRINT",FACE,{"disambiguationData":[TD([[makeQuery(id+"F47.imprint","IMPRINT",EDGE,{"derivedFrom":subQ0}),-1.0]])]})])],"isStart":true});}
            var Q2;
            {var subQ0=sQuery(id+"F51.wireOp",EDGE,"E98");Q2=makeQuery(id+"F51.imprint","IMPRINT",FACE,{"disambiguationData":[TD([[makeQuery(id+"F51.imprint","IMPRINT",EDGE,{"derivedFrom":subQ0}),-1.0]])]});}
            loft(context, id + "F59", {"operationType" : NewBodyOperationType.ADD, "sheetProfilesArray" : [{ "sheetProfileEntities" : qUnion([Q1]) }, { "sheetProfileEntities" : qUnion([Q2]) }]});
        }
        {
            var Q1;
            {var subQ0=sQuery(id+"F49.wireOp",EDGE,"E96");Q1=makeQuery(id+"F58.opLoft","CAP_FACE",FACE,{"disambiguationData":[OSD([makeQuery(id+"F49.imprint","IMPRINT",FACE,{"disambiguationData":[TD([[makeQuery(id+"F49.imprint","IMPRINT",EDGE,{"derivedFrom":subQ0}),-1.0]])]})])],"isStart":true});}
            var Q2;
            {var subQ0=sQuery(id+"F53.wireOp",EDGE,"E100");Q2=makeQuery(id+"F53.imprint","IMPRINT",FACE,{"disambiguationData":[TD([[makeQuery(id+"F53.imprint","IMPRINT",EDGE,{"derivedFrom":subQ0}),-1.0]])]});}
            loft(context, id + "F60", {"operationType" : NewBodyOperationType.ADD, "sheetProfilesArray" : [{ "sheetProfileEntities" : qUnion([Q1]) }, { "sheetProfileEntities" : qUnion([Q2]) }]});
        }
    });
